# Revit family: Window-Treatment_Pleated_SWFcontract_Pleated
name_source: partatom
category: Specialty Equipment
units: mm (PartAtom-declared; Revit-internal decimal feet)

## family parameters
Always vertical = No
Classification Number = 23.30.60.14
Cut with Voids When Loaded = No
Enable Cutting in Views = No
Maintain Annotation Orientation = No
Part Type = Normal
Room Calculation Point = No
Round Connector Dimension = Use Diameter
Shared = No
Work Plane-Based = Yes

## types (1)
- Window-Treatment_Pleated_SWFcontract_Pleated
    Assembly Code = E2010300
    Cell Spacing = 0' - 1 1/4"
    Construction Details = http://www.arcat.com
    Default Elevation = 0' - 0"
    Description = SWFcontract Window Treatment as Specified
    Double Cell Construction = No
    Expected Lifespan (Years) = 0
    Green Building-LEED = http://www.arcat.com
    Header Depth = 0' - 1 17/32"
    Header Height = 0' - 0 21/32"
    Keynote = 12490
    Large Single Cell Construction = Yes
    Maintenance Schedule (Months) = 0
    Manufacturer = SWFcontract
    Manufacturer Website = http://www.swfcontract.com
    Model = As Specified
    Product Data = http://www.arcat.com
    Revision = R1_03-2014
    Sales Information = http://www.swfcontract.com
    Send Message = http://www.arcat.com
    Small Single Cell Construction = No
    SpecWizard = http://www.arcat.com
    Specification = http://www.arcat.com
    URL = http://www.swfcontract.com
    Unit Height = 4' - 0"
    Unit Width = 4' - 0"
    Warranty Duration (Years) = 0
    handlelength = 2' - 6"

## geometry (parser evidence)
native form markers: Blend x4, Sweep x6
no freeform markers — native parametric forms only
